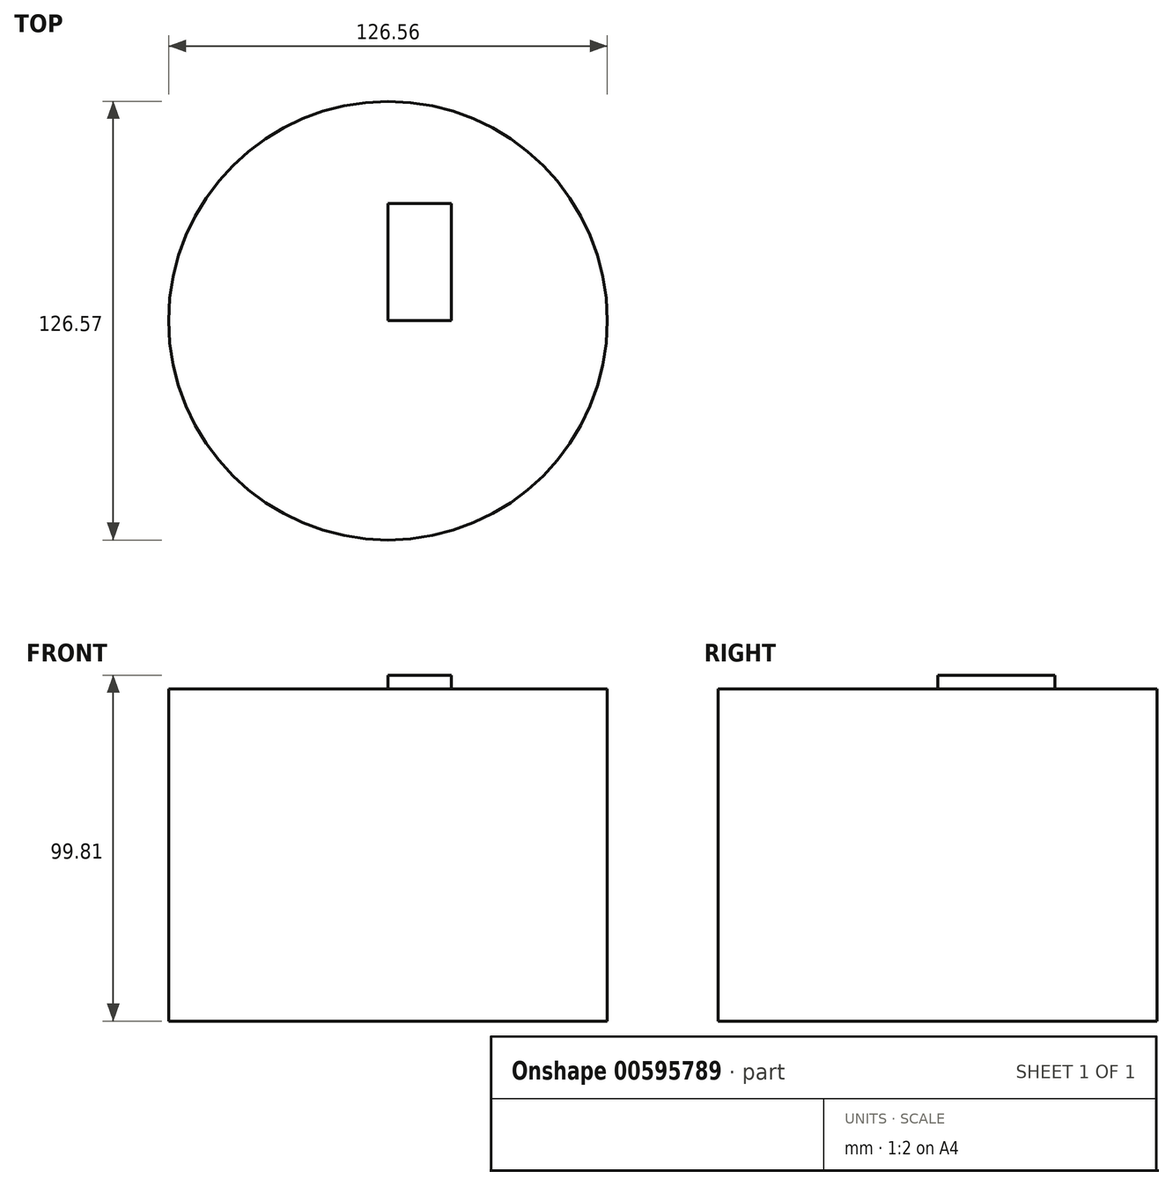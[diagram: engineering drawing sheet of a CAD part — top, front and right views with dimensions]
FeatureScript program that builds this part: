
annotation { "Feature Type Name" : "Feature", "Feature Type Description" : "" }
export const myFeature = defineFeature(function(context is Context, id is Id, definition is map)
    precondition{}
    {
        {
            var Q0;
            Q0=qCreatedBy(makeId("Top.planeOp"),FACE);
            var sketch = newSketch(context, id + "F0", { "sketchPlane" : qUnion([Q0])});
            skCircle(sketch, "E0", {"center": v(0, 50.23) * mm, "radius": 63.28 * mm});
            skSolve(sketch);
        }
        {
            var Q0;
            Q0=makeQuery(id+"F0.imprint","IMPRINT",FACE,{"disambiguationData":[TD([[makeQuery(id+"F0.imprint","IMPRINT",EDGE,{"derivedFrom":sQuery(id+"F0.wireOp",EDGE,"E0")}),1.0]])]});
            extrude(context, id + "F1", {"entities" : qUnion([Q0]), "depth" : 95.78 * mm, "offsetDistance" : 25.4 * mm});
        }
        {
            var Q0;
            Q0=makeQuery(id+"F1.opExtrude","CAP_FACE",FACE,{"disambiguationData":[OSD([sQuery(id+"F0.wireOp",EDGE,"E0")])],"isStart":false});
            var sketch = newSketch(context, id + "F2", { "sketchPlane" : qUnion([Q0])});
            skLineSegment(sketch, "E1.bottom", {"start": v(0, 50.23) * mm, "end": v(18.32, 50.23) * mm});
            skLineSegment(sketch, "E1.top", {"start": v(0, 84.02) * mm, "end": v(18.32, 84.02) * mm});
            skLineSegment(sketch, "E1.left", {"start": v(0, 50.23) * mm, "end": v(0, 84.02) * mm});
            skLineSegment(sketch, "E1.right", {"start": v(18.32, 50.23) * mm, "end": v(18.32, 84.02) * mm});
            skSolve(sketch);
        }
        {
            var Q0;
            Q0 = qSketchRegion(id + "F2", true);
            extrude(context, id + "F3", {"entities" : qUnion([Q0]), "operationType" : NewBodyOperationType.ADD, "depth" : 4.03 * mm, "offsetDistance" : 25.4 * mm});
        }
    });
